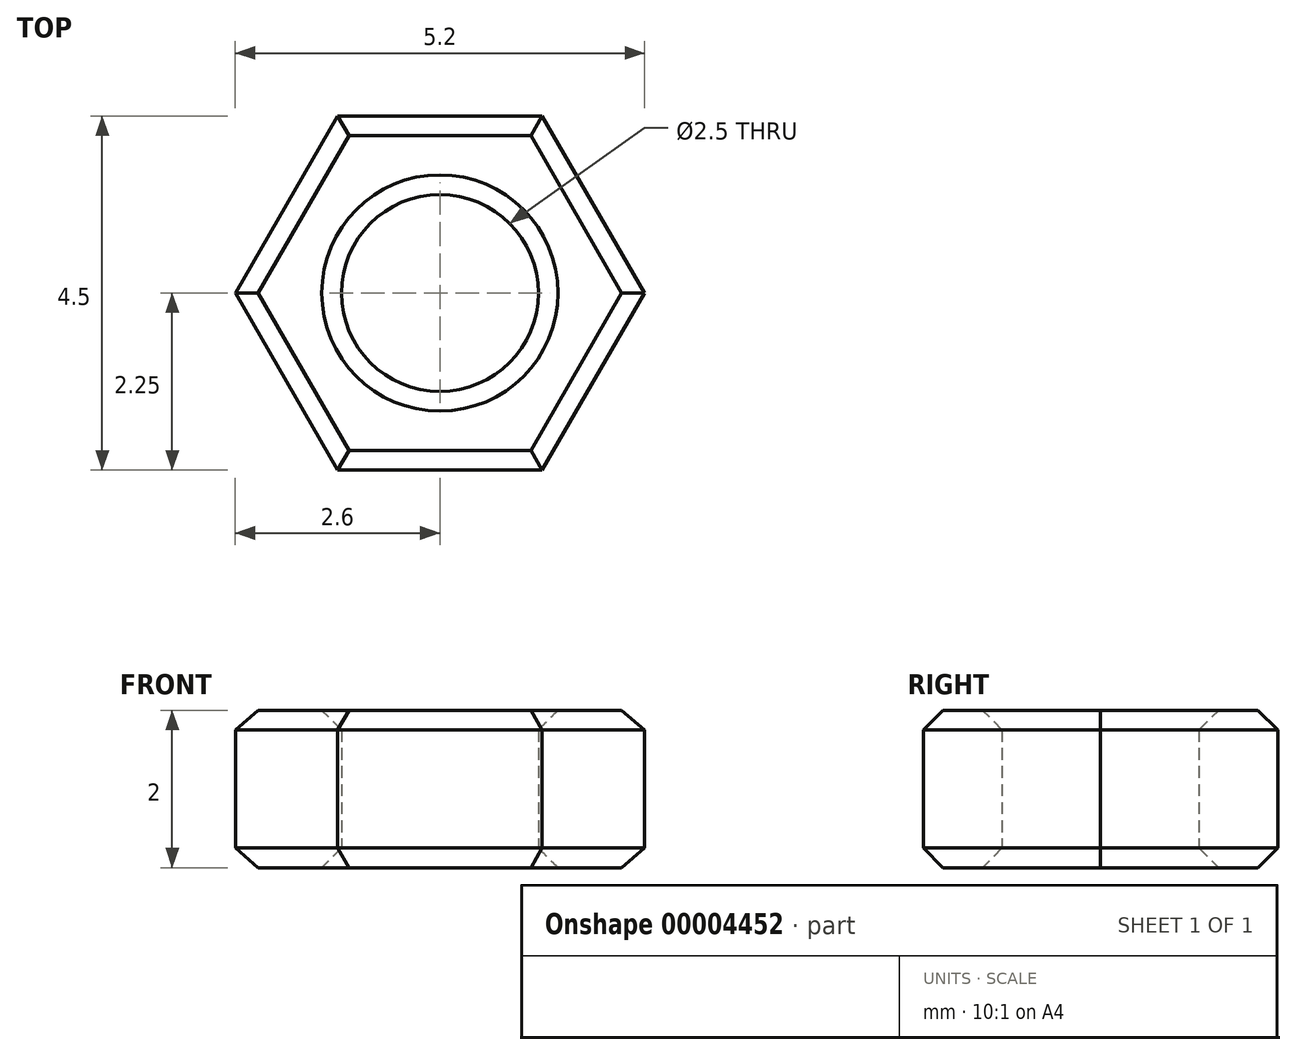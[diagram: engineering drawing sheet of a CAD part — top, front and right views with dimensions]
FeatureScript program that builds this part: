
annotation { "Feature Type Name" : "Feature", "Feature Type Description" : "" }
export const myFeature = defineFeature(function(context is Context, id is Id, definition is map)
    precondition{}
    {
        {
            var Q0;
            Q0=qCreatedBy(makeId("Top.planeOp"),FACE);
            var sketch = newSketch(context, id + "F0", { "sketchPlane" : qUnion([Q0])});
            skCircle(sketch, "E0", {"center": v(0, 0) * mm, "radius": 1.25 * mm});
            skCircle(sketch, "E1.cCircle", {"center": v(0, 0) * mm, "radius": 2.25 * mm, "construction": true});
            skLineSegment(sketch, "E1.0", {"start": v(-1.3, 2.25) * mm, "end": v(1.3, 2.25) * mm});
            skLineSegment(sketch, "E1.1", {"start": v(1.3, 2.25) * mm, "end": v(2.6, 0) * mm});
            skLineSegment(sketch, "E1.2", {"start": v(2.6, 0) * mm, "end": v(1.3, -2.25) * mm});
            skLineSegment(sketch, "E1.3", {"start": v(1.3, -2.25) * mm, "end": v(-1.3, -2.25) * mm});
            skLineSegment(sketch, "E1.4", {"start": v(-1.3, -2.25) * mm, "end": v(-2.6, 0) * mm});
            skLineSegment(sketch, "E1.5", {"start": v(-2.6, 0) * mm, "end": v(-1.3, 2.25) * mm});
            skPoint(sketch, "E1.0.midPoint", {"position": v(0, 2.25) * mm});
            skSolve(sketch);
        }
        {
            var Q0;
            Q0=makeQuery(id+"F0.imprint","IMPRINT",FACE,{"disambiguationData":[TD([[makeQuery(id+"F0.imprint","IMPRINT",EDGE,{"derivedFrom":sQuery(id+"F0.wireOp",EDGE,"E0")}),-1.0]])]});
            extrude(context, id + "F1", {"entities" : qUnion([Q0]), "depth" : 2 * mm});
        }
        {
            var Q0;
            Q0=makeQuery(id+"F1.opExtrude","CAP_FACE",FACE,{"disambiguationData":[OSD([sQuery(id+"F0.wireOp",EDGE,"E0"),sQuery(id+"F0.wireOp",EDGE,"E1.0"),sQuery(id+"F0.wireOp",EDGE,"E1.1"),sQuery(id+"F0.wireOp",EDGE,"E1.2"),sQuery(id+"F0.wireOp",EDGE,"E1.3"),sQuery(id+"F0.wireOp",EDGE,"E1.4"),sQuery(id+"F0.wireOp",EDGE,"E1.5")])],"isStart":false});
            var Q1;
            Q1=makeQuery(id+"F1.opExtrude","CAP_FACE",FACE,{"disambiguationData":[OSD([sQuery(id+"F0.wireOp",EDGE,"E0"),sQuery(id+"F0.wireOp",EDGE,"E1.0"),sQuery(id+"F0.wireOp",EDGE,"E1.1"),sQuery(id+"F0.wireOp",EDGE,"E1.2"),sQuery(id+"F0.wireOp",EDGE,"E1.3"),sQuery(id+"F0.wireOp",EDGE,"E1.4"),sQuery(id+"F0.wireOp",EDGE,"E1.5")])],"isStart":true});
            chamfer(context, id + "F2", {"entities" : qUnion([Q0, Q1]), "width" : .25 * mm, "tangentPropagation" : true});
        }
    });
